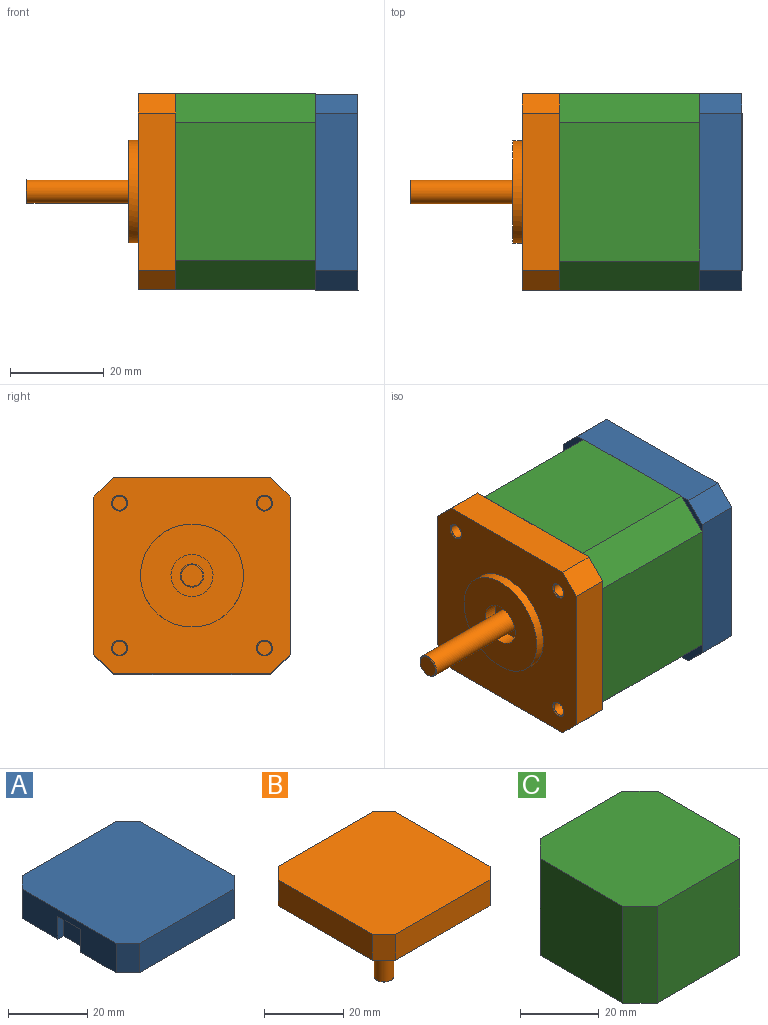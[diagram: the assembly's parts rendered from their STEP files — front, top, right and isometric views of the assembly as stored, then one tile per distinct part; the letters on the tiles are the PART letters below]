
ASSEMBLY  parts=3 mates=2
PART A: 14 faces, bbox 42x42x9 mm
  f0: plane 33.6x9mm, normal (1,0,0), area 302.4mm2, adj f4,f5,f6,f7
  f1: plane 33.6x9mm, normal (0,1,0), area 302.4mm2, adj f4,f5,f6,f9
  f2: plane 33.6x9mm, normal (-1,0,0), area 246.4mm2, adj f4,f5,f8,f9,f10,f11,f12
  f3: plane 33.6x9mm, normal (0,-1,0), area 302.4mm2, adj f4,f5,f7,f8
  f4: plane 42x42mm, normal (0,0,1), area 1728.7mm2, adj f0,f1,f2,f3,f6,f7,f8,f9
  f5: plane 42x42mm, normal (0,0,-1), area 1712.7mm2, adj f0,f1,f2,f3,f6,f7,f8,f9
  f6: plane 9x4.2mm, normal (0.71,0.71,0), area 53.5mm2, adj f0,f1,f4,f5
  f7: plane 9x4.2mm, normal (0.71,-0.71,0), area 53.5mm2, adj f0,f3,f4,f5
  f8: plane 9x4.2mm, normal (-0.71,-0.71,0), area 53.5mm2, adj f2,f3,f4,f5
  f9: plane 9x4.2mm, normal (-0.71,0.71,0), area 53.5mm2, adj f1,f2,f4,f5
  f10: plane 8x2mm, normal (0,0,-1), area 16mm2, adj f2,f11,f12,f13
  f11: plane 7x2mm, normal (0,1,0), area 14mm2, adj f2,f5,f10,f13
  f12: plane 7x2mm, normal (0,-1,0), area 14mm2, adj f2,f5,f10,f13
  f13: plane 8x7mm, normal (-1,0,0), area 56mm2, adj f5,f10,f11,f12
PART B: 29 faces, bbox 42x42x32 mm
  f0: plane 9x9mm, normal (0,0,-1), area 44mm2, adj f13,f14
  f1: plane 42x42mm, normal (0,0,-1), area 1312.3mm2, adj f2,f3,f4,f5,f7,f8,f9,f10
  f2: plane 33.6x8mm, normal (1,0,0), area 268.8mm2, adj f1,f6,f9,f10
  f3: plane 33.6x8mm, normal (0,1,0), area 268.8mm2, adj f1,f6,f8,f9
  f4: plane 33.6x8mm, normal (-1,0,0), area 268.8mm2, adj f1,f6,f7,f8
  f5: plane 33.6x8mm, normal (0,-1,0), area 268.8mm2, adj f1,f6,f7,f10
  f6: plane 42x42mm, normal (0,0,1), area 1728.7mm2, adj f2,f3,f4,f5,f7,f8,f9,f10
  f7: plane 8x4.2mm, normal (-0.71,-0.71,0), area 47.5mm2, adj f1,f4,f5,f6
  f8: plane 8x4.2mm, normal (-0.71,0.71,0), area 47.5mm2, adj f1,f3,f4,f6
  f9: plane 8x4.2mm, normal (0.71,0.71,0), area 47.5mm2, adj f1,f2,f3,f6
  f10: plane 8x4.2mm, normal (0.71,-0.71,0), area 47.5mm2, adj f1,f2,f5,f6
  f11: cylinder r=11mm len=22mm, axis (0,0,1), area 138.2mm2, adj f1,f12
  f12: plane 22x22mm, normal (0,0,-1), area 316.5mm2, adj f11,f13
  f13: cylinder r=4.5mm len=9mm, axis (0,0,-1), area 84.8mm2, adj f0,f12
  f14: cylinder r=2.5mm len=24.8mm, axis (0,0,1), area 389.6mm2, adj f0,f16
  f15: plane 4.6x4.6mm, normal (0,0,-1), area 16.6mm2, adj f16
  f16: cone r=2.3mm half-angle=45deg, axis (0,0,1), area 4.3mm2, adj f14,f15
  f17: cylinder r=1.5mm len=4.8mm, axis (0,0,-1), area 45.2mm2, adj f18,f28
  f18: plane 3x3mm, normal (0,0,-1), area 7.1mm2, adj f17
  f19: cylinder r=1.5mm len=4.8mm, axis (0,0,-1), area 45.2mm2, adj f20,f27
  f20: plane 3x3mm, normal (0,0,-1), area 7.1mm2, adj f19
  f21: cylinder r=1.5mm len=4.8mm, axis (0,0,-1), area 45.2mm2, adj f22,f26
  f22: plane 3x3mm, normal (0,0,-1), area 7.1mm2, adj f21
  f23: cylinder r=1.5mm len=4.8mm, axis (0,0,-1), area 45.2mm2, adj f24,f25
  f24: plane 3x3mm, normal (0,0,-1), area 7.1mm2, adj f23
  f25: cone r=1.5mm half-angle=45deg, axis (0,0,-1), area 2.8mm2, adj f1,f23
  f26: cone r=1.5mm half-angle=45deg, axis (0,0,-1), area 2.8mm2, adj f1,f21
  f27: cone r=1.5mm half-angle=45deg, axis (0,0,-1), area 2.8mm2, adj f1,f19
  f28: cone r=1.5mm half-angle=45deg, axis (0,0,-1), area 2.8mm2, adj f1,f17
PART C: 10 faces, bbox 42x42x30 mm
  f0: plane 30x29.6mm, normal (0,1,0), area 888mm2, adj f1,f7,f8,f9
  f1: plane 30x6.2mm, normal (-0.71,0.71,0), area 263mm2, adj f0,f2,f8,f9
  f2: plane 30x29.6mm, normal (-1,0,0), area 888mm2, adj f1,f3,f8,f9
  f3: plane 30x6.2mm, normal (-0.71,-0.71,0), area 263mm2, adj f2,f4,f8,f9
  f4: plane 30x29.6mm, normal (0,-1,0), area 888mm2, adj f3,f5,f8,f9
  f5: plane 30x6.2mm, normal (0.71,-0.71,0), area 263mm2, adj f4,f6,f8,f9
  f6: plane 30x29.6mm, normal (1,0,0), area 888mm2, adj f5,f7,f8,f9
  f7: plane 30x6.2mm, normal (0.71,0.71,0), area 263mm2, adj f0,f6,f8,f9
  f8: plane 42x42mm, normal (0,0,1), area 1687.1mm2, adj f0,f1,f2,f3,f4,f5,f6,f7
  f9: plane 42x42mm, normal (0,0,-1), area 1687.1mm2, adj f0,f1,f2,f3,f4,f5,f6,f7
PLACE A rot(axis=(-0.71,0,-0.71),180deg) t=(102.18,58.42,-10.92)mm
PLACE B rot(axis=(-0.71,0,-0.71),180deg) t=(102.18,58.42,-10.73)mm
PLACE C rot(axis=(-0.71,0,-0.71),180deg) t=(102.18,58.42,-10.73)mm
MATE fastened A.f5 <-> C.f8  axis (-1,0,0) through (140.18,58.42,-10.73)mm
MATE fastened C.f9 <-> B.f11  axis (-1,0,0) through (110.18,58.42,-10.73)mm
